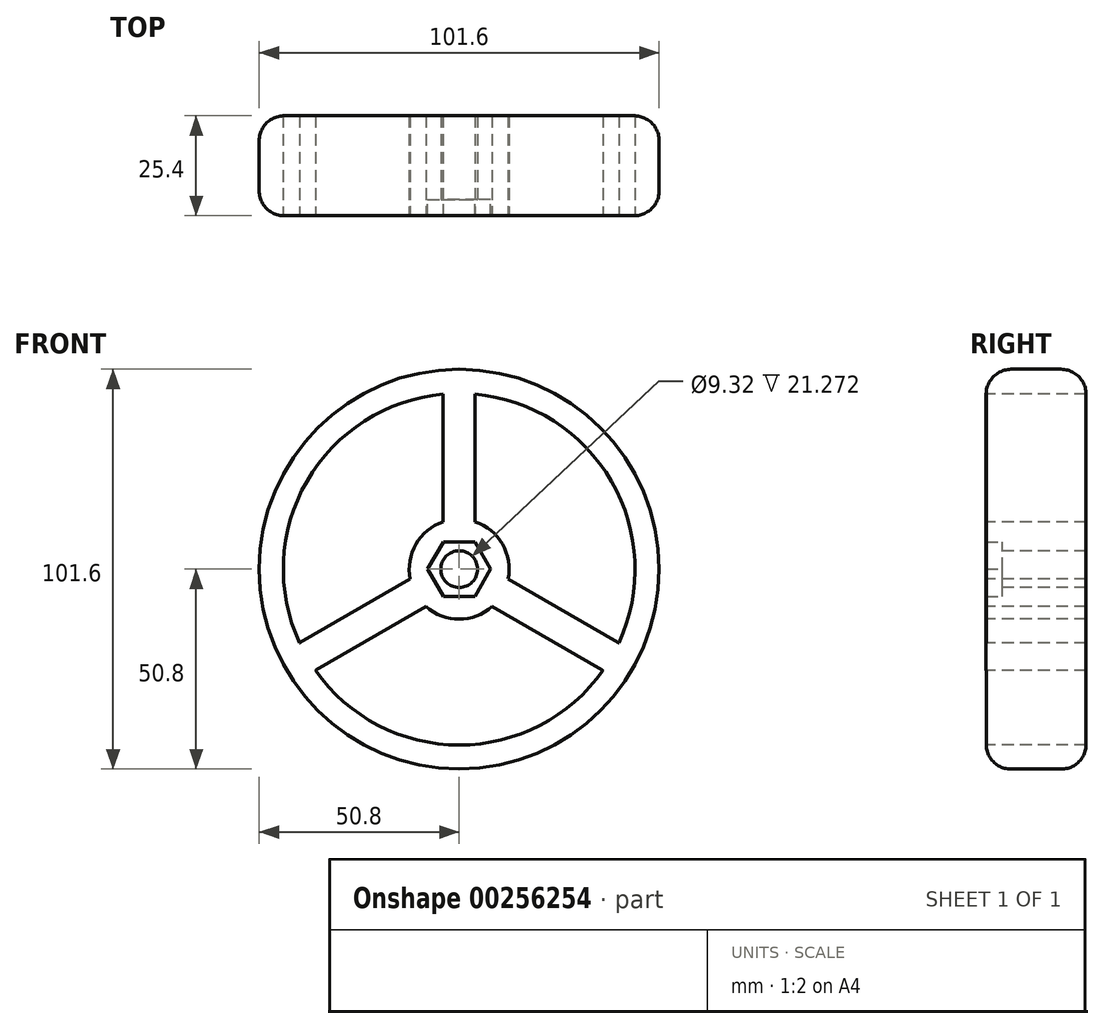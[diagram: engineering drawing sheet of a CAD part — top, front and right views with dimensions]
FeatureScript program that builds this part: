
annotation { "Feature Type Name" : "Feature", "Feature Type Description" : "" }
export const myFeature = defineFeature(function(context is Context, id is Id, definition is map)
    precondition{}
    {
        {
            var Q0;
            Q0=qCreatedBy(makeId("Front.planeOp"),FACE);
            var sketch = newSketch(context, id + "F0", { "sketchPlane" : qUnion([Q0])});
            skCircle(sketch, "E0", {"center": v(0, 0) * mm, "radius": 50.8 * mm});
            skSolve(sketch);
        }
        {
            var Q0;
            Q0=makeQuery(id+"F0.imprint","IMPRINT",FACE,{"disambiguationData":[TD([[makeQuery(id+"F0.imprint","IMPRINT",EDGE,{"derivedFrom":sQuery(id+"F0.wireOp",EDGE,"E0")}),1.0]])]});
            extrude(context, id + "F1", {"entities" : qUnion([Q0]), "depth" : 25.4 * mm});
        }
        {
            var Q0;
            Q0=makeQuery(id+"F1.opExtrude","CAP_FACE",FACE,{"disambiguationData":[OSD([sQuery(id+"F0.wireOp",EDGE,"E0")])],"isStart":false});
            var sketch = newSketch(context, id + "F2", { "sketchPlane" : qUnion([Q0])});
            skCircle(sketch, "E1", {"center": v(0, 0) * mm, "radius": 12.7 * mm});
            skSolve(sketch);
        }
        {
            var Q0;
            Q0=makeQuery(id+"F2.imprint","IMPRINT",FACE,{"disambiguationData":[TD([[makeQuery(id+"F2.imprint","IMPRINT",EDGE,{"derivedFrom":sQuery(id+"F2.wireOp",EDGE,"E1")}),1.0]])]});
            var sketch = newSketch(context, id + "F3", { "sketchPlane" : qUnion([Q0])});
            skCircle(sketch, "E2.cCircle", {"center": v(0, 0) * mm, "radius": 6.93 * mm, "construction": true});
            skLineSegment(sketch, "E2.0", {"start": v(-4, 6.93) * mm, "end": v(4, 6.93) * mm});
            skLineSegment(sketch, "E2.1", {"start": v(4, 6.93) * mm, "end": v(8, 0) * mm});
            skLineSegment(sketch, "E2.2", {"start": v(8, 0) * mm, "end": v(4, -6.93) * mm});
            skLineSegment(sketch, "E2.3", {"start": v(4, -6.93) * mm, "end": v(-4, -6.93) * mm});
            skLineSegment(sketch, "E2.4", {"start": v(-4, -6.93) * mm, "end": v(-8, 0) * mm});
            skLineSegment(sketch, "E2.5", {"start": v(-8, 0) * mm, "end": v(-4, 6.93) * mm});
            skPoint(sketch, "E2.0.midPoint", {"position": v(0, 6.93) * mm});
            skSolve(sketch);
        }
        {
            var Q0;
            Q0 = qSketchRegion(id + "F3", true);
            extrude(context, id + "F4", {"entities" : qUnion([Q0]), "operationType" : NewBodyOperationType.REMOVE, "endBound" : BoundingType.SYMMETRIC, "depth" : 8.25 * mm});
        }
        {
            var Q0;
            Q0=makeQuery(id+"F2.imprint","IMPRINT",FACE,{"disambiguationData":[TD([[makeQuery(id+"F2.imprint","IMPRINT",EDGE,{"derivedFrom":sQuery(id+"F2.wireOp",EDGE,"E1")}),1.0]])]});
            var sketch = newSketch(context, id + "F5", { "sketchPlane" : qUnion([Q0])});
            skCircle(sketch, "E3", {"center": v(0, 0) * mm, "radius": 4.66 * mm});
            skSolve(sketch);
        }
        {
            var Q0;
            Q0 = qSketchRegion(id + "F5", true);
            extrude(context, id + "F6", {"entities" : qUnion([Q0]), "operationType" : NewBodyOperationType.REMOVE, "endBound" : BoundingType.THROUGH_ALL, "oppositeDirection" : true, "depth" : 50.8 * mm});
        }
        {
            var Q0;
            Q0=makeQuery(id+"F1.opExtrude","CAP_EDGE",EDGE,{"disambiguationData":[OSD([sQuery(id+"F0.wireOp",EDGE,"E0")])],"isStart":false});
            var Q1;
            Q1=makeQuery(id+"F1.opExtrude","CAP_EDGE",EDGE,{"disambiguationData":[OSD([sQuery(id+"F0.wireOp",EDGE,"E0")])],"isStart":true});
            fillet(context, id + "F7", {"entities" : qUnion([Q0, Q1]), "radius" : 6.35 * mm, "tangentPropagation" : true, "allowEdgeOverflow" : false});
        }
        {
            var Q0;
            Q0=makeQuery(id+"F2.imprint","IMPRINT",FACE,{"disambiguationData":[TD([[makeQuery(id+"F2.imprint","IMPRINT",EDGE,{"derivedFrom":sQuery(id+"F2.wireOp",EDGE,"E1")}),-1.0]])]});
            var sketch = newSketch(context, id + "F8", { "sketchPlane" : qUnion([Q0])});
            skCircle(sketch, "E4.cCircle", {"center": v(0, 0) * mm, "radius": 8.1 * mm, "construction": true});
            skLineSegment(sketch, "E4.0", {"start": v(4.05, 7.01) * mm, "end": v(8.1, 0) * mm});
            skLineSegment(sketch, "E4.1", {"start": v(8.1, 0) * mm, "end": v(4.05, -7.01) * mm});
            skLineSegment(sketch, "E4.2", {"start": v(4.05, -7.01) * mm, "end": v(-4.05, -7.01) * mm});
            skLineSegment(sketch, "E4.3", {"start": v(-4.05, -7.01) * mm, "end": v(-8.1, 0) * mm});
            skLineSegment(sketch, "E4.4", {"start": v(-8.1, 0) * mm, "end": v(-4.05, 7.01) * mm});
            skLineSegment(sketch, "E4.5", {"start": v(-4.05, 7.01) * mm, "end": v(4.05, 7.01) * mm});
            skCircle(sketch, "E5", {"center": v(0, 0) * mm, "radius": 44.68 * mm});
            skLineSegment(sketch, "E6", {"start": v(4.05, 7.01) * mm, "end": v(4.05, 44.5) * mm});
            skLineSegment(sketch, "E7", {"start": v(-4.05, 7.01) * mm, "end": v(-4.05, 44.5) * mm});
            skLineSegment(sketch, "E8.1.0", {"start": v(-8.1, 0) * mm, "end": v(-40.56, -18.74) * mm});
            skLineSegment(sketch, "E8.1.1", {"start": v(-4.05, -7.01) * mm, "end": v(-36.5, -25.75) * mm});
            skLineSegment(sketch, "E8.2.0", {"start": v(4.05, -7.01) * mm, "end": v(36.5, -25.75) * mm});
            skLineSegment(sketch, "E8.2.1", {"start": v(8.1, 0) * mm, "end": v(40.56, -18.74) * mm});
            skSolve(sketch);
        }
        {
            var Q0;
            {var subQ0=sQuery(id+"F8.wireOp",EDGE,"E6");var subQ1=sQuery(id+"F8.wireOp",EDGE,"E5");var subQ2=makeQuery(id+"F8.imprint","INTERSECT",VERTEX,{"derivedFrom":[subQ1,subQ0]});Q0=makeQuery(id+"F8.imprint","IMPRINT",FACE,{"disambiguationData":[TD([[makeQuery(id+"F8.imprint","IMPRINT",EDGE,{"disambiguationData":[TD([[subQ2,1.0]])],"derivedFrom":subQ1}),1.0]])]});}
            var Q1;
            {var subQ0=sQuery(id+"F8.wireOp",EDGE,"E7");var subQ1=sQuery(id+"F8.wireOp",EDGE,"E5");var subQ2=makeQuery(id+"F8.imprint","INTERSECT",VERTEX,{"derivedFrom":[subQ1,subQ0]});Q1=makeQuery(id+"F8.imprint","IMPRINT",FACE,{"disambiguationData":[TD([[makeQuery(id+"F8.imprint","IMPRINT",EDGE,{"disambiguationData":[TD([[subQ2,-1.0]])],"derivedFrom":subQ1}),1.0]])]});}
            var Q2;
            {var subQ0=sQuery(id+"F8.wireOp",EDGE,"E8.1.1");var subQ1=sQuery(id+"F8.wireOp",EDGE,"E5");var subQ2=makeQuery(id+"F8.imprint","INTERSECT",VERTEX,{"derivedFrom":[subQ1,subQ0]});Q2=makeQuery(id+"F8.imprint","IMPRINT",FACE,{"disambiguationData":[TD([[makeQuery(id+"F8.imprint","IMPRINT",EDGE,{"disambiguationData":[TD([[subQ2,-1.0]])],"derivedFrom":subQ1}),1.0]])]});}
            extrude(context, id + "F9", {"entities" : qUnion([Q0, Q1, Q2]), "operationType" : NewBodyOperationType.REMOVE, "endBound" : BoundingType.UP_TO_NEXT, "oppositeDirection" : true, "depth" : 25.4 * mm});
        }
    });
